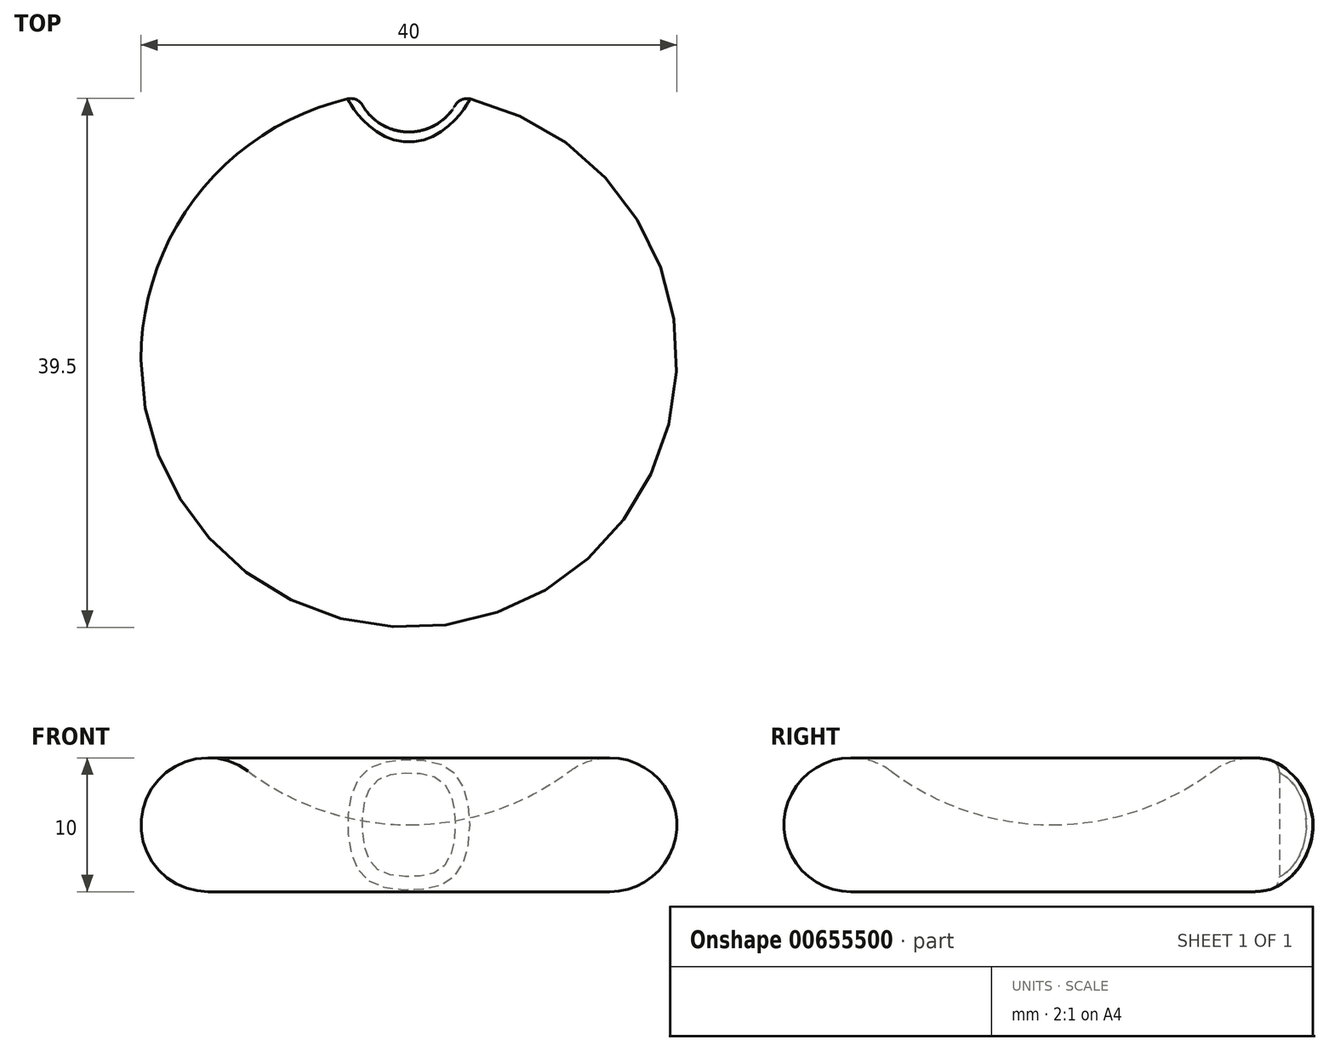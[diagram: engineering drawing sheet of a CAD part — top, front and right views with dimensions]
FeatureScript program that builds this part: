
annotation { "Feature Type Name" : "Feature", "Feature Type Description" : "" }
export const myFeature = defineFeature(function(context is Context, id is Id, definition is map)
    precondition{}
    {
        {
            var Q0;
            Q0=qCreatedBy(makeId("Front.planeOp"),FACE);
            var sketch = newSketch(context, id + "F0", { "sketchPlane" : qUnion([Q0])});
            skArc(sketch, "E0", {"start": v(-12, 9) * mm, "mid": v(-19.74, 6.58) * mm, "end": v(-15, 0) * mm});
            skArc(sketch, "E1", {"start": v(-12, 9) * mm, "mid": v(-6.32, 6.03) * mm, "end": v(0, 5) * mm});
            skLineSegment(sketch, "E2", {"start": v(-15, 0) * mm, "end": v(0, 0) * mm});
            skLineSegment(sketch, "E3", {"start": v(0, 0) * mm, "end": v(0, 5) * mm});
            skPoint(sketch, "E4.orphan", {"position": v(-9.4, 0) * mm});
            skSolve(sketch);
        }
        {
            var Q0;
            Q0=makeQuery(id+"F0.imprint","IMPRINT",FACE,{"disambiguationData":[TD([[makeQuery(id+"F0.imprint","IMPRINT",EDGE,{"derivedFrom":sQuery(id+"F0.wireOp",EDGE,"E0")}),1.0]])]});
            var Q1;
            Q1=sQuery(id+"F0.wireOp",EDGE,"E3");
            revolve(context, id + "F1", {"entities" : qUnion([Q0]), "axis" : qUnion([Q1]), "revolveType" : RevolveType.FULL});
        }
        {
            var Q0;
            Q0=qCreatedBy(makeId("Top.planeOp"),FACE);
            var sketch = newSketch(context, id + "F2", { "sketchPlane" : qUnion([Q0])});
            skCircle(sketch, "E5", {"center": v(0, 21) * mm, "radius": 4 * mm});
            skSolve(sketch);
        }
        {
            var Q0;
            Q0=makeQuery(id+"F2.imprint","IMPRINT",FACE,{"disambiguationData":[TD([[makeQuery(id+"F2.imprint","IMPRINT",EDGE,{"derivedFrom":sQuery(id+"F2.wireOp",EDGE,"E5")}),1.0]])]});
            extrude(context, id + "F3", {"entities" : qUnion([Q0]), "operationType" : NewBodyOperationType.REMOVE, "depth" : 25 * mm, "offsetDistance" : 25.4 * mm});
        }
        {
            var Q0;
            Q0=makeQuery(id+"F3.boolean.opBoolean","INTERSECT",EDGE,{"derivedFrom":[makeQuery(id+"F1.opRevolve","SWEPT_FACE",FACE,{"disambiguationData":[OSD([sQuery(id+"F0.wireOp",EDGE,"E0")])]}),makeQuery(id+"F3.opExtrude","SWEPT_FACE",FACE,{"disambiguationData":[OSD([sQuery(id+"F2.wireOp",EDGE,"E5")])]})]});
            fillet(context, id + "F4", {"entities" : qUnion([Q0]), "radius" : 1 * mm, "tangentPropagation" : true, "allowEdgeOverflow" : false});
        }
    });
